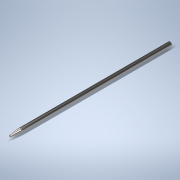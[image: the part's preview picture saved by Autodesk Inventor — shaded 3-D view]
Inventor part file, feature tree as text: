
AUTODESK INVENTOR PART (.ipt)
format: ipt  version: 2021 (Build 250183000, 183)  size: 99,328 bytes
history: native  units: mm
features: other x1, extrude x1, chamfer x1, sketch x1
ambient origin geometry x8: Origin, YZ Plane, XZ Plane, XY Plane, X Axis, Y Axis, Z Axis, Center Point
bodies: Body1 (feature_tree)
feature tree (4):
  other  "Bryła1"
  extrude  "Wyciągnięcie proste1"  Depth=4.0mm
  chamfer  "Faza1"  Distance=160.0mm
  sketch  "Szkic1"
